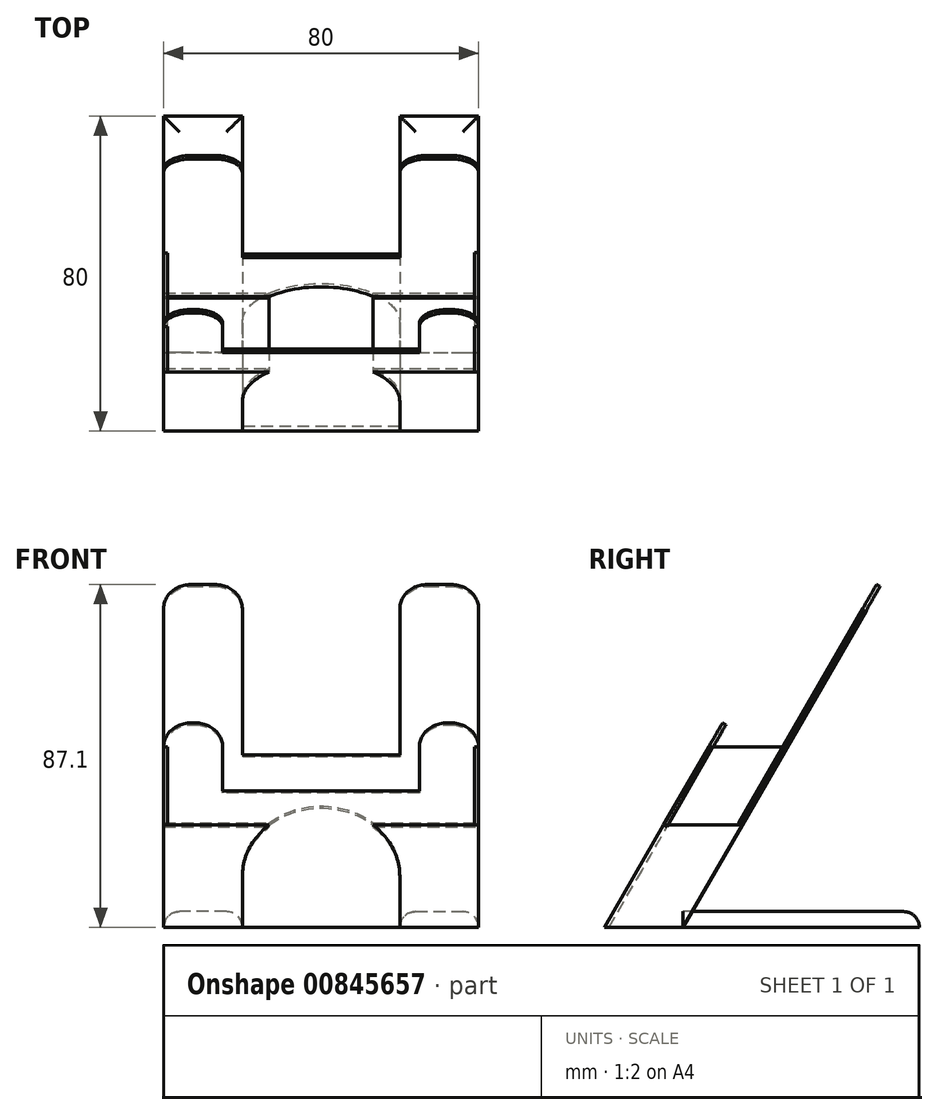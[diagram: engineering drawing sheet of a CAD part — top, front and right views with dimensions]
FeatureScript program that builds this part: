
annotation { "Feature Type Name" : "Feature", "Feature Type Description" : "" }
export const myFeature = defineFeature(function(context is Context, id is Id, definition is map)
    precondition{}
    {
        {
            var Q0;
            Q0=qCreatedBy(makeId("Top.planeOp"),FACE);
            var sketch = newSketch(context, id + "F0", { "sketchPlane" : qUnion([Q0])});
            skLineSegment(sketch, "E0.bottom", {"start": v(-40, 40) * mm, "end": v(-20, 40) * mm});
            skLineSegment(sketch, "E0.top", {"start": v(-40, -40) * mm, "end": v(40, -40) * mm});
            skLineSegment(sketch, "E0.left", {"start": v(-40, 40) * mm, "end": v(-40, -40) * mm});
            skLineSegment(sketch, "E0.right", {"start": v(40, 40) * mm, "end": v(40, -40) * mm});
            skPoint(sketch, "E0.middle", {"position": v(0, 0) * mm});
            skLineSegment(sketch, "E1.bottom", {"start": v(-20, 40) * mm, "end": v(-20, 40) * mm});
            skLineSegment(sketch, "E1.top", {"start": v(-20, -20) * mm, "end": v(20, -20) * mm});
            skLineSegment(sketch, "E1.left", {"start": v(-20, 40) * mm, "end": v(-20, -20) * mm});
            skLineSegment(sketch, "E1.right", {"start": v(20, 40) * mm, "end": v(20, 40) * mm});
            skLineSegment(sketch, "E2.bottom", {"start": v(20, -20) * mm, "end": v(-20, -20) * mm});
            skLineSegment(sketch, "E2.top", {"start": v(20, -38) * mm, "end": v(-20, -38) * mm});
            skLineSegment(sketch, "E2.left", {"start": v(20, -20) * mm, "end": v(20, -38) * mm});
            skLineSegment(sketch, "E2.right", {"start": v(-20, -20) * mm, "end": v(-20, -38) * mm});
            skLineSegment(sketch, "E3", {"start": v(-20, -20) * mm, "end": v(-40, -20) * mm});
            skLineSegment(sketch, "E4", {"start": v(20, -20) * mm, "end": v(40, -20) * mm});
            skLineSegment(sketch, "E5", {"start": v(20, 40) * mm, "end": v(20, -20) * mm});
            skLineSegment(sketch, "E6.trimOffspring", {"start": v(20, 40) * mm, "end": v(40, 40) * mm});
            skSolve(sketch);
        }
        {
            var Q0;
            Q0=sQuery(id+"F0.wireOp",EDGE,"E0.top");
            cPlane(context, id + "F1", {"entities" : qUnion([Q0]), "cplaneType" : CPlaneType.LINE_ANGLE, "offset" : 25 * mm, "angle" : 30 * degree, "oppositeDirection" : true, "width" : 150 * mm, "height" : 150 * mm});
        }
        {
            var Q0;
            Q0=qCreatedBy(id+"F1.planeOp",FACE);
            var sketch = newSketch(context, id + "F2", { "sketchPlane" : qUnion([Q0])});
            skLineSegment(sketch, "E7.bottom", {"start": v(40, -20) * mm, "end": v(-40, -20) * mm});
            skLineSegment(sketch, "E7.top", {"start": v(40, 40) * mm, "end": v(-40, 40) * mm});
            skLineSegment(sketch, "E7.left", {"start": v(40, -20) * mm, "end": v(40, 40) * mm});
            skLineSegment(sketch, "E7.right", {"start": v(-40, -20) * mm, "end": v(-40, 40) * mm});
            skLineSegment(sketch, "E8.bottom", {"start": v(-25, 40) * mm, "end": v(25, 40) * mm});
            skLineSegment(sketch, "E8.top", {"start": v(-25, 20) * mm, "end": v(25, 20) * mm});
            skLineSegment(sketch, "E8.left", {"start": v(-25, 40) * mm, "end": v(-25, 20) * mm});
            skLineSegment(sketch, "E8.right", {"start": v(25, 40) * mm, "end": v(25, 20) * mm});
            skLineSegment(sketch, "E9", {"start": v(40, 10) * mm, "end": v(13.23, 10) * mm});
            skLineSegment(sketch, "E10.bottom", {"start": v(20, -20) * mm, "end": v(-20, -20) * mm});
            skLineSegment(sketch, "E10.top", {"start": v(0, 15) * mm, "end": v(0, 15) * mm});
            skLineSegment(sketch, "E10.left", {"start": v(20, -20) * mm, "end": v(20, -5) * mm});
            skLineSegment(sketch, "E10.right", {"start": v(-20, -20) * mm, "end": v(-20, -5) * mm});
            skPoint(sketch, "E11.visualSharp", {"position": v(20, 15) * mm});
            skArc(sketch, "E11.filletArc", {"start": v(20, -5) * mm, "mid": v(18.23, 3.23) * mm, "end": v(13.23, 10) * mm});
            skPoint(sketch, "E12.visualSharp", {"position": v(-20, 15) * mm});
            skLineSegment(sketch, "E13", {"start": v(13.23, 10) * mm, "end": v(-13.23, 10) * mm});
            skLineSegment(sketch, "E14", {"start": v(-13.23, 10) * mm, "end": v(-40, 10) * mm});
            skArc(sketch, "E15", {"start": v(-13.23, 10) * mm, "mid": v(-18.23, 3.23) * mm, "end": v(-20, -5) * mm});
            skSolve(sketch);
        }
        {
            var Q0;
            Q0=sQuery(id+"F0.wireOp",EDGE,"E1.top");
            cPlane(context, id + "F3", {"entities" : qUnion([Q0]), "cplaneType" : CPlaneType.LINE_ANGLE, "offset" : 25 * mm, "angle" : 30 * degree, "oppositeDirection" : true, "width" : 150 * mm, "height" : 150 * mm});
        }
        {
            var Q0;
            Q0=qCreatedBy(id+"F3.planeOp",FACE);
            var sketch = newSketch(context, id + "F4", { "sketchPlane" : qUnion([Q0])});
            skLineSegment(sketch, "E16.bottom", {"start": v(40, -10) * mm, "end": v(-40, -10) * mm});
            skLineSegment(sketch, "E16.top", {"start": v(40, 90) * mm, "end": v(-40, 90) * mm});
            skLineSegment(sketch, "E16.left", {"start": v(40, -10) * mm, "end": v(40, 90) * mm});
            skLineSegment(sketch, "E16.right", {"start": v(-40, -10) * mm, "end": v(-40, 90) * mm});
            skLineSegment(sketch, "E17.bottom", {"start": v(-20, 90) * mm, "end": v(20, 90) * mm});
            skLineSegment(sketch, "E17.top", {"start": v(-20, 40) * mm, "end": v(20, 40) * mm});
            skLineSegment(sketch, "E17.left", {"start": v(-20, 90) * mm, "end": v(-20, 40) * mm});
            skLineSegment(sketch, "E17.right", {"start": v(20, 90) * mm, "end": v(20, 40) * mm});
            skLineSegment(sketch, "E18.bottom", {"start": v(-20, -10) * mm, "end": v(20, -10) * mm});
            skLineSegment(sketch, "E18.top", {"start": v(0, 25) * mm, "end": v(0, 25) * mm});
            skLineSegment(sketch, "E18.left", {"start": v(-20, -10) * mm, "end": v(-20, 5) * mm});
            skLineSegment(sketch, "E18.right", {"start": v(20, -10) * mm, "end": v(20, 5) * mm});
            skPoint(sketch, "E19.visualSharp", {"position": v(-20, 25) * mm});
            skArc(sketch, "E19.filletArc", {"start": v(0, 25) * mm, "mid": v(-14.14, 19.14) * mm, "end": v(-20, 5) * mm});
            skPoint(sketch, "E20.visualSharp", {"position": v(20, 25) * mm});
            skArc(sketch, "E20.filletArc", {"start": v(20, 5) * mm, "mid": v(14.14, 19.14) * mm, "end": v(0, 25) * mm});
            skLineSegment(sketch, "E21", {"start": v(40, 20) * mm, "end": v(13.23, 20) * mm});
            skLineSegment(sketch, "E22", {"start": v(-13.23, 20) * mm, "end": v(-40, 20) * mm});
            skSolve(sketch);
        }
        {
            var Q0;
            {var subQ0=sQuery(id+"F4.wireOp",EDGE,"E18.right");Q0=makeQuery(id+"F4.imprint","IMPRINT",FACE,{"disambiguationData":[TD([[makeQuery(id+"F4.imprint","IMPRINT",EDGE,{"derivedFrom":subQ0}),-1.0]])]});}
            var Q1;
            {var subQ1=sQuery(id+"F2.wireOp",EDGE,"E9");Q1=makeQuery(id+"F2.imprint","IMPRINT",FACE,{"disambiguationData":[TD([[makeQuery(id+"F2.imprint","IMPRINT",EDGE,{"derivedFrom":subQ1}),1.0]])]});}
            loft(context, id + "F5", {"sheetProfilesArray" : [{ "sheetProfileEntities" : qUnion([Q0]) }, { "sheetProfileEntities" : qUnion([Q1]) }]});
        }
        {
            var Q0;
            {var subQ1=sQuery(id+"F4.wireOp",EDGE,"E18.left");Q0=makeQuery(id+"F4.imprint","IMPRINT",FACE,{"disambiguationData":[TD([[makeQuery(id+"F4.imprint","IMPRINT",EDGE,{"derivedFrom":subQ1}),1.0]])]});}
            var Q1;
            {var subQ0=sQuery(id+"F2.wireOp",EDGE,"E10.right");Q1=makeQuery(id+"F2.imprint","IMPRINT",FACE,{"disambiguationData":[TD([[makeQuery(id+"F2.imprint","IMPRINT",EDGE,{"derivedFrom":subQ0}),1.0]])]});}
            loft(context, id + "F6", {"sheetProfilesArray" : [{ "sheetProfileEntities" : qUnion([Q0]) }, { "sheetProfileEntities" : qUnion([Q1]) }]});
        }
        {
            var Q0;
            Q0=makeQuery(id+"F4.imprint","IMPRINT",FACE,{"disambiguationData":[TD([[makeQuery(id+"F4.imprint","IMPRINT",EDGE,{"derivedFrom":sQuery(id+"F4.wireOp",EDGE,"E17.top")}),-1.0]])]});
            extrude(context, id + "F7", {"entities" : qUnion([Q0]), "oppositeDirection" : true, "depth" : 1 * mm, "offsetDistance" : 25 * mm});
        }
        {
            var Q0;
            Q0=makeQuery(id+"F7.opExtrude","SWEPT_FACE",FACE,{"disambiguationData":[OSD([sQuery(id+"F4.wireOp",EDGE,"E21")])]});
            var Q1;
            Q1=makeQuery(id+"F5.opLoft","SWEPT_FACE",FACE,{"disambiguationData":[OSD([sQuery(id+"F2.wireOp",EDGE,"E7.left"),sQuery(id+"F2.wireOp",EDGE,"E9"),sQuery(id+"F2.wireOp",EDGE,"E11.filletArc"),sQuery(id+"F2.wireOp",EDGE,"E13"),sQuery(id+"F4.wireOp",EDGE,"E16.left"),sQuery(id+"F4.wireOp",EDGE,"E20.filletArc"),sQuery(id+"F4.wireOp",EDGE,"E21")])]});
            extrude(context, id + "F8", {"entities" : qUnion([Q0]), "endBound" : BoundingType.UP_TO_SURFACE, "depth" : 25 * mm, "endBoundEntityFace" : qUnion([Q1]), "offsetDistance" : 25 * mm});
        }
        {
            var Q0;
            Q0=makeQuery(id+"F7.opExtrude","SWEPT_FACE",FACE,{"disambiguationData":[OSD([sQuery(id+"F4.wireOp",EDGE,"E22")])]});
            var Q1;
            Q1=makeQuery(id+"F6.opLoft","SWEPT_FACE",FACE,{"disambiguationData":[OSD([sQuery(id+"F2.wireOp",EDGE,"E7.right"),sQuery(id+"F2.wireOp",EDGE,"E13"),sQuery(id+"F2.wireOp",EDGE,"E14"),sQuery(id+"F2.wireOp",EDGE,"E15"),sQuery(id+"F4.wireOp",EDGE,"E16.right"),sQuery(id+"F4.wireOp",EDGE,"E19.filletArc"),sQuery(id+"F4.wireOp",EDGE,"E22")])]});
            extrude(context, id + "F9", {"entities" : qUnion([Q0]), "endBound" : BoundingType.UP_TO_SURFACE, "depth" : 25 * mm, "endBoundEntityFace" : qUnion([Q1]), "offsetDistance" : 25 * mm});
        }
        {
            var Q0;
            {var subQ0=sQuery(id+"F2.wireOp",EDGE,"E10.left");Q0=makeQuery(id+"F2.imprint","IMPRINT",FACE,{"disambiguationData":[TD([[makeQuery(id+"F2.imprint","IMPRINT",EDGE,{"derivedFrom":subQ0}),1.0]])]});}
            var Q1;
            Q1=makeQuery(id+"F2.imprint","IMPRINT",FACE,{"disambiguationData":[TD([[makeQuery(id+"F2.imprint","IMPRINT",EDGE,{"derivedFrom":sQuery(id+"F2.wireOp",EDGE,"E8.top")}),-1.0]])]});
            extrude(context, id + "F10", {"entities" : qUnion([Q0, Q1]), "depth" : 1 * mm, "offsetDistance" : 25 * mm});
        }
        {
            var Q0;
            Q0=makeQuery(id+"F10.opExtrude","CAP_EDGE",EDGE,{"disambiguationData":[OSD([sQuery(id+"F2.wireOp",EDGE,"E7.bottom")])],"isStart":false});
            chamfer(context, id + "F11", {"entities" : qUnion([Q0]), "chamferType" : ChamferType.OFFSET_ANGLE, "width" : 1 * mm, "oppositeDirection" : false, "angle" : 30 * degree, "tangentPropagation" : true});
        }
        {
            var Q0;
            {var subQ3=sQuery(id+"F0.wireOp",EDGE,"E1.left");Q0=makeQuery(id+"F0.imprint","IMPRINT",FACE,{"disambiguationData":[TD([[makeQuery(id+"F0.imprint","IMPRINT",EDGE,{"derivedFrom":subQ3}),-1.0]])]});}
            var Q1;
            {var subQ3=sQuery(id+"F0.wireOp",EDGE,"E1.right");Q1=makeQuery(id+"F0.imprint","IMPRINT",FACE,{"disambiguationData":[TD([[makeQuery(id+"F0.imprint","IMPRINT",EDGE,{"derivedFrom":subQ3}),1.0]])]});}
            var Q2;
            {var subQ2=sQuery(id+"F0.wireOp",EDGE,"E4");Q2=makeQuery(id+"F0.imprint","IMPRINT",FACE,{"disambiguationData":[TD([[makeQuery(id+"F0.imprint","IMPRINT",EDGE,{"derivedFrom":subQ2}),1.0]])]});}
            extrude(context, id + "F12", {"entities" : qUnion([Q0, Q1, Q2]), "depth" : 4 * mm, "offsetDistance" : 25 * mm});
        }
        {
            var Q0;
            Q0=makeQuery(id+"F12.opExtrude","CAP_EDGE",EDGE,{"disambiguationData":[OSD([sQuery(id+"F0.wireOp",EDGE,"E0.right")])],"isStart":false});
            var Q1;
            Q1=makeQuery(id+"F12.opExtrude","CAP_EDGE",EDGE,{"disambiguationData":[OSD([sQuery(id+"F0.wireOp",EDGE,"E1.right")])],"isStart":false});
            var Q2;
            Q2=makeQuery(id+"F12.opExtrude","CAP_EDGE",EDGE,{"disambiguationData":[OSD([sQuery(id+"F0.wireOp",EDGE,"E1.left")])],"isStart":false});
            var Q3;
            Q3=makeQuery(id+"F12.opExtrude","CAP_EDGE",EDGE,{"disambiguationData":[OSD([sQuery(id+"F0.wireOp",EDGE,"E0.left")])],"isStart":false});
            var Q4;
            {var subQ0=sQuery(id+"F0.wireOp",EDGE,"E0.bottom");Q4=makeQuery(id+"F12.opExtrude","CAP_EDGE",EDGE,{"disambiguationData":[OSD([subQ0]),TDD([makeQuery(id+"F0.imprint","IMPRINT",EDGE,{"disambiguationData":[TD([[makeQuery(id+"F0.imprint","INTERSECT",VERTEX,{"derivedFrom":[subQ0,sQuery(id+"F0.wireOp",EDGE,"E0.right")]}),1.0]])],"derivedFrom":subQ0})])],"isStart":false});}
            var Q5;
            {var subQ0=sQuery(id+"F0.wireOp",EDGE,"E0.bottom");Q5=makeQuery(id+"F12.opExtrude","CAP_EDGE",EDGE,{"disambiguationData":[OSD([subQ0]),TDD([makeQuery(id+"F0.imprint","IMPRINT",EDGE,{"disambiguationData":[TD([[makeQuery(id+"F0.imprint","INTERSECT",VERTEX,{"derivedFrom":[subQ0,sQuery(id+"F0.wireOp",EDGE,"E0.left")]}),-1.0]])],"derivedFrom":subQ0})])],"isStart":false});}
            var Q6;
            Q6=makeQuery(id+"F12.opExtrude","CAP_EDGE",EDGE,{"disambiguationData":[OSD([sQuery(id+"F0.wireOp",EDGE,"E5")])],"isStart":false});
            var Q7;
            Q7=makeQuery(id+"F12.opExtrude","CAP_EDGE",EDGE,{"disambiguationData":[OSD([sQuery(id+"F0.wireOp",EDGE,"E6.trimOffspring")])],"isStart":false});
            fillet(context, id + "F13", {"entities" : qUnion([Q0, Q1, Q2, Q3, Q4, Q5, Q6, Q7]), "radius" : 4 * mm, "tangentPropagation" : true, "allowEdgeOverflow" : false});
        }
        {
            var Q0;
            Q0=makeQuery(id+"F10.opExtrude","SWEPT_EDGE",EDGE,{"disambiguationData":[OSD([sQuery(id+"F2.wireOp",EDGE,"E7.top"),sQuery(id+"F2.wireOp",EDGE,"E7.left")])]});
            var Q1;
            Q1=makeQuery(id+"F10.opExtrude","SWEPT_EDGE",EDGE,{"disambiguationData":[OSD([sQuery(id+"F2.wireOp",EDGE,"E7.top"),sQuery(id+"F2.wireOp",EDGE,"E8.right")])]});
            var Q2;
            Q2=makeQuery(id+"F7.opExtrude","SWEPT_EDGE",EDGE,{"disambiguationData":[OSD([sQuery(id+"F4.wireOp",EDGE,"E16.top"),sQuery(id+"F4.wireOp",EDGE,"E16.left")])]});
            var Q3;
            Q3=makeQuery(id+"F7.opExtrude","SWEPT_EDGE",EDGE,{"disambiguationData":[OSD([sQuery(id+"F4.wireOp",EDGE,"E16.top"),sQuery(id+"F4.wireOp",EDGE,"E17.right")])]});
            var Q4;
            Q4=makeQuery(id+"F10.opExtrude","SWEPT_EDGE",EDGE,{"disambiguationData":[OSD([sQuery(id+"F2.wireOp",EDGE,"E7.top"),sQuery(id+"F2.wireOp",EDGE,"E8.left")])]});
            var Q5;
            Q5=makeQuery(id+"F7.opExtrude","SWEPT_EDGE",EDGE,{"disambiguationData":[OSD([sQuery(id+"F4.wireOp",EDGE,"E16.top"),sQuery(id+"F4.wireOp",EDGE,"E17.left")])]});
            var Q6;
            Q6=makeQuery(id+"F10.opExtrude","SWEPT_EDGE",EDGE,{"disambiguationData":[OSD([sQuery(id+"F2.wireOp",EDGE,"E7.top"),sQuery(id+"F2.wireOp",EDGE,"E7.right")])]});
            var Q7;
            Q7=makeQuery(id+"F7.opExtrude","SWEPT_EDGE",EDGE,{"disambiguationData":[OSD([sQuery(id+"F4.wireOp",EDGE,"E16.top"),sQuery(id+"F4.wireOp",EDGE,"E16.right")])]});
            fillet(context, id + "F14", {"entities" : qUnion([Q0, Q1, Q2, Q3, Q4, Q5, Q6, Q7]), "radius" : 7 * mm, "tangentPropagation" : true, "allowEdgeOverflow" : false});
        }
        {
            var Q0;
            Q0=makeQuery(id+"F5.opLoft","SWEPT_FACE",FACE,{"disambiguationData":[OSD([sQuery(id+"F2.wireOp",EDGE,"E7.bottom"),sQuery(id+"F2.wireOp",EDGE,"E7.left"),sQuery(id+"F2.wireOp",EDGE,"E9"),sQuery(id+"F4.wireOp",EDGE,"E16.bottom"),sQuery(id+"F4.wireOp",EDGE,"E16.left"),sQuery(id+"F4.wireOp",EDGE,"E21")])]});
            cPlane(context, id + "F15", {"entities" : qUnion([Q0]), "cplaneType" : CPlaneType.OFFSET, "offset" : 0 * mm, "width" : 150 * mm, "height" : 150 * mm});
        }
        {
            var Q0;
            Q0=qCreatedBy(id+"F15.planeOp",FACE);
            var sketch = newSketch(context, id + "F16", { "sketchPlane" : qUnion([Q0])});
            skLineSegment(sketch, "E23", {"start": v(13.5, 45.9) * mm, "end": v(-5.27, 45.9) * mm});
            skLineSegment(sketch, "E24", {"start": v(13.5, 45.9) * mm, "end": v(25, 25.98) * mm});
            skLineSegment(sketch, "E25", {"start": v(25, 25.98) * mm, "end": v(6.15, 25.98) * mm});
            skLineSegment(sketch, "E26", {"start": v(6.15, 25.98) * mm, "end": v(-5.27, 45.9) * mm});
            skSolve(sketch);
        }
        {
            var Q0;
            Q0=makeQuery(id+"F16.imprint","IMPRINT",FACE,{"disambiguationData":[TD([[makeQuery(id+"F16.imprint","IMPRINT",EDGE,{"derivedFrom":sQuery(id+"F16.wireOp",EDGE,"E23")}),1.0]])]});
            extrude(context, id + "F17", {"entities" : qUnion([Q0]), "oppositeDirection" : true, "depth" : 1 * mm, "offsetDistance" : 25 * mm});
        }
        {
            var Q0;
            Q0=makeQuery(id+"F6.opLoft","SWEPT_FACE",FACE,{"disambiguationData":[OSD([sQuery(id+"F2.wireOp",EDGE,"E7.bottom"),sQuery(id+"F2.wireOp",EDGE,"E7.right"),sQuery(id+"F2.wireOp",EDGE,"E14"),sQuery(id+"F4.wireOp",EDGE,"E16.bottom"),sQuery(id+"F4.wireOp",EDGE,"E16.right"),sQuery(id+"F4.wireOp",EDGE,"E22")])]});
            cPlane(context, id + "F18", {"entities" : qUnion([Q0]), "cplaneType" : CPlaneType.OFFSET, "offset" : 0 * mm, "width" : 150 * mm, "height" : 150 * mm});
        }
        {
            var Q0;
            Q0=qCreatedBy(id+"F18.planeOp",FACE);
            var sketch = newSketch(context, id + "F19", { "sketchPlane" : qUnion([Q0])});
            skLineSegment(sketch, "E27", {"start": v(-25, 25.98) * mm, "end": v(-6.15, 25.98) * mm});
            skLineSegment(sketch, "E28", {"start": v(-6.15, 25.98) * mm, "end": v(5.35, 45.9) * mm});
            skLineSegment(sketch, "E29", {"start": v(5.35, 45.9) * mm, "end": v(-13.5, 45.9) * mm});
            skLineSegment(sketch, "E30", {"start": v(-13.5, 45.9) * mm, "end": v(-25, 25.98) * mm});
            skSolve(sketch);
        }
        {
            var Q0;
            Q0=makeQuery(id+"F19.imprint","IMPRINT",FACE,{"disambiguationData":[TD([[makeQuery(id+"F19.imprint","IMPRINT",EDGE,{"derivedFrom":sQuery(id+"F19.wireOp",EDGE,"E27")}),1.0]])]});
            extrude(context, id + "F20", {"entities" : qUnion([Q0]), "oppositeDirection" : true, "depth" : 1 * mm, "offsetDistance" : 25 * mm});
        }
    });
